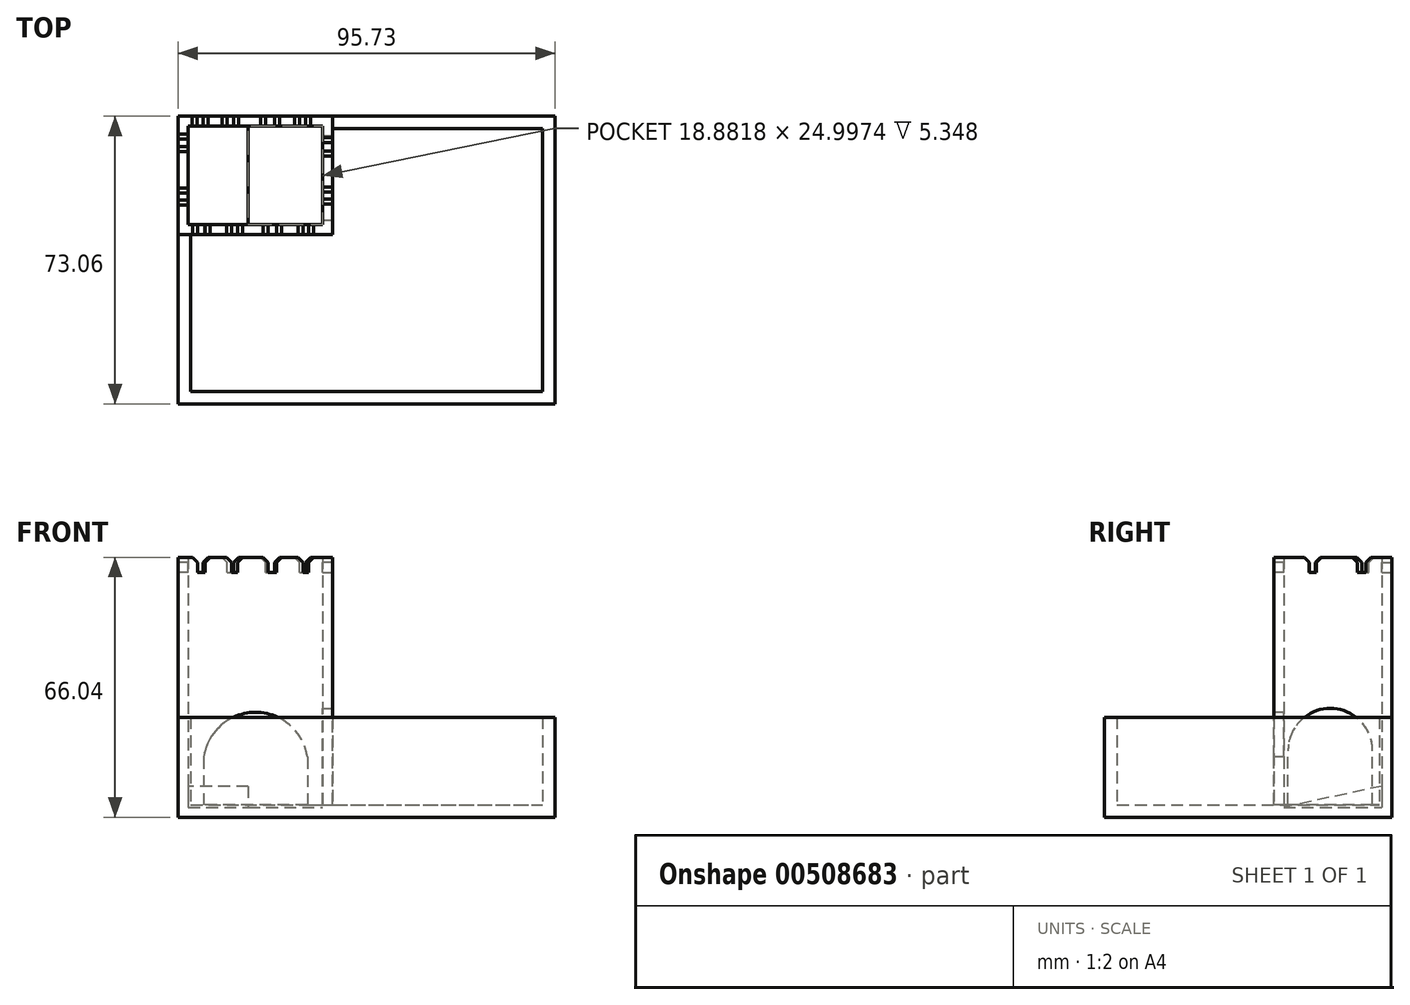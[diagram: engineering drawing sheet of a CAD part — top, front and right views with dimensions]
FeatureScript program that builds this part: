
annotation { "Feature Type Name" : "Feature", "Feature Type Description" : "" }
export const myFeature = defineFeature(function(context is Context, id is Id, definition is map)
    precondition{}
    {
        {
            var Q0;
            Q0=qCreatedBy(makeId("Top.planeOp"),FACE);
            var sketch = newSketch(context, id + "F0", { "sketchPlane" : qUnion([Q0])});
            skLineSegment(sketch, "E0.bottom", {"start": v(-43.95, -29.63) * mm, "end": v(51.78, -29.63) * mm});
            skLineSegment(sketch, "E0.top", {"start": v(-43.95, 43.43) * mm, "end": v(51.78, 43.43) * mm});
            skLineSegment(sketch, "E0.left", {"start": v(-43.95, -29.63) * mm, "end": v(-43.95, 43.43) * mm});
            skLineSegment(sketch, "E0.right", {"start": v(51.78, -29.63) * mm, "end": v(51.78, 43.43) * mm});
            skSolve(sketch);
        }
        {
            var Q0;
            Q0=makeQuery(id+"F0.imprint","IMPRINT",FACE,{"disambiguationData":[TD([[makeQuery(id+"F0.imprint","IMPRINT",EDGE,{"derivedFrom":sQuery(id+"F0.wireOp",EDGE,"E0.bottom")}),1.0]])]});
            extrude(context, id + "F1", {"entities" : qUnion([Q0]), "depth" : 25.4 * mm});
        }
        {
            var Q0;
            Q0=makeQuery(id+"F1.opExtrude","CAP_FACE",FACE,{"disambiguationData":[OSD([sQuery(id+"F0.wireOp",EDGE,"E0.bottom"),sQuery(id+"F0.wireOp",EDGE,"E0.top"),sQuery(id+"F0.wireOp",EDGE,"E0.left"),sQuery(id+"F0.wireOp",EDGE,"E0.right")])],"isStart":false});
            shell(context, id + "F2", {"entities" : qUnion([Q0]), "thickness" : 3.17 * mm});
        }
        {
            var Q0;
            Q0=makeQuery(id+"F2.opShell","OFFSET_FACE",FACE,{"disambiguationData":[OSD([sQuery(id+"F0.wireOp",EDGE,"E0.bottom"),sQuery(id+"F0.wireOp",EDGE,"E0.top"),sQuery(id+"F0.wireOp",EDGE,"E0.left"),sQuery(id+"F0.wireOp",EDGE,"E0.right")])]});
            var sketch = newSketch(context, id + "F3", { "sketchPlane" : qUnion([Q0])});
            skLineSegment(sketch, "E1.bottom", {"start": v(-40.77, 40.26) * mm, "end": v(-4.75, 40.26) * mm});
            skLineSegment(sketch, "E1.top", {"start": v(-40.77, 13.35) * mm, "end": v(-4.75, 13.35) * mm});
            skLineSegment(sketch, "E1.left", {"start": v(-40.77, 40.26) * mm, "end": v(-40.77, 13.35) * mm});
            skLineSegment(sketch, "E1.right", {"start": v(-4.75, 40.26) * mm, "end": v(-4.75, 13.35) * mm});
            skSolve(sketch);
        }
        {
            var Q0;
            Q0 = qSketchRegion(id + "F3", true);
            var Q1;
            Q1=makeQuery(id+"F3.imprint","IMPRINT",FACE,{"disambiguationData":[TD([[makeQuery(id+"F3.imprint","IMPRINT",EDGE,{"derivedFrom":sQuery(id+"F3.wireOp",EDGE,"E1.bottom")}),-1.0]])]});
            extrude(context, id + "F4", {"entities" : qUnion([Q0, Q1]), "operationType" : NewBodyOperationType.ADD, "depth" : 22.22 * mm});
        }
        {
            var Q0;
            Q0=makeQuery(id+"F4.boolean.opBoolean","MERGE",FACE,{"derivedFrom":[makeQuery(id+"F1.opExtrude","CAP_FACE",FACE,{"disambiguationData":[OSD([sQuery(id+"F0.wireOp",EDGE,"E0.bottom"),sQuery(id+"F0.wireOp",EDGE,"E0.top"),sQuery(id+"F0.wireOp",EDGE,"E0.left"),sQuery(id+"F0.wireOp",EDGE,"E0.right")])],"isStart":false}),makeQuery(id+"F4.opExtrude","CAP_FACE",FACE,{"disambiguationData":[OSD([sQuery(id+"F3.wireOp",EDGE,"E1.bottom"),sQuery(id+"F3.wireOp",EDGE,"E1.top"),sQuery(id+"F3.wireOp",EDGE,"E1.left"),sQuery(id+"F3.wireOp",EDGE,"E1.right")])],"isStart":false})]});
            var sketch = newSketch(context, id + "F5", { "sketchPlane" : qUnion([Q0])});
            skLineSegment(sketch, "E2", {"start": v(-40.77, 13.35) * mm, "end": v(-43.95, 13.35) * mm});
            skLineSegment(sketch, "E3", {"start": v(-4.75, 40.26) * mm, "end": v(-4.75, 43.43) * mm});
            skSolve(sketch);
        }
        {
            var Q0;
            Q0 = qSketchRegion(id + "F5", true);
            var Q1;
            {var subQ1=sQuery(id+"F5.wireOp",EDGE,"E2");Q1=makeQuery(id+"F5.imprint","IMPRINT",FACE,{"disambiguationData":[TD([[makeQuery(id+"F5.imprint","IMPRINT",EDGE,{"derivedFrom":subQ1}),-1.0]])]});}
            extrude(context, id + "F6", {"entities" : qUnion([Q0, Q1]), "operationType" : NewBodyOperationType.ADD, "depth" : 38.1 * mm});
        }
        {
            var Q0;
            Q0=makeQuery(id+"F6.opExtrude","CAP_FACE",FACE,{"disambiguationData":[OSD([sQuery(id+"F0.wireOp",EDGE,"E0.top"),sQuery(id+"F0.wireOp",EDGE,"E0.left"),sQuery(id+"F3.wireOp",EDGE,"E1.top"),sQuery(id+"F3.wireOp",EDGE,"E1.right"),sQuery(id+"F5.wireOp",EDGE,"E2"),sQuery(id+"F5.wireOp",EDGE,"E3")])],"isStart":false});
            shell(context, id + "F7", {"entities" : qUnion([Q0]), "thickness" : 2.54 * mm});
        }
        {
            var Q0;
            {var subQ0=sQuery(id+"F3.wireOp",EDGE,"E1.top");Q0=makeQuery(id+"F6.boolean.opBoolean","MERGE",FACE,{"derivedFrom":[makeQuery(id+"F4.opExtrude","SWEPT_FACE",FACE,{"disambiguationData":[OSD([subQ0])]}),makeQuery(id+"F6.opExtrude","SWEPT_FACE",FACE,{"disambiguationData":[OSD([subQ0,sQuery(id+"F5.wireOp",EDGE,"E2")])]})]});}
            var sketch = newSketch(context, id + "F8", { "sketchPlane" : qUnion([Q0])});
            skLineSegment(sketch, "E4.bottom", {"start": v(-37.47, 3.18) * mm, "end": v(-11.12, 3.18) * mm});
            skLineSegment(sketch, "E4.top", {"start": v(-37.47, 15.27) * mm, "end": v(-11.12, 15.27) * mm});
            skLineSegment(sketch, "E4.left", {"start": v(-37.47, 3.18) * mm, "end": v(-37.47, 15.27) * mm});
            skLineSegment(sketch, "E4.right", {"start": v(-11.12, 3.18) * mm, "end": v(-11.12, 15.27) * mm});
            skArc(sketch, "E5", {"start": v(-11.12, 15.27) * mm, "mid": v(-24.3, 26.67) * mm, "end": v(-37.47, 15.27) * mm});
            skSolve(sketch);
        }
        {
            var Q0;
            Q0=makeQuery(id+"F8.imprint","IMPRINT",FACE,{"disambiguationData":[TD([[makeQuery(id+"F8.imprint","IMPRINT",EDGE,{"derivedFrom":sQuery(id+"F8.wireOp",EDGE,"E4.top")}),1.0]])]});
            var Q1;
            Q1=makeQuery(id+"F8.imprint","IMPRINT",FACE,{"disambiguationData":[TD([[makeQuery(id+"F8.imprint","IMPRINT",EDGE,{"derivedFrom":sQuery(id+"F8.wireOp",EDGE,"E4.bottom")}),1.0]])]});
            extrude(context, id + "F9", {"entities" : qUnion([Q0, Q1]), "operationType" : NewBodyOperationType.REMOVE, "oppositeDirection" : true, "depth" : 3.17 * mm});
        }
        {
            var Q0;
            {var subQ0=sQuery(id+"F3.wireOp",EDGE,"E1.right");Q0=makeQuery(id+"F6.boolean.opBoolean","MERGE",FACE,{"derivedFrom":[makeQuery(id+"F4.opExtrude","SWEPT_FACE",FACE,{"disambiguationData":[OSD([subQ0])]}),makeQuery(id+"F6.opExtrude","SWEPT_FACE",FACE,{"disambiguationData":[OSD([subQ0,sQuery(id+"F5.wireOp",EDGE,"E3")])]})]});}
            var sketch = newSketch(context, id + "F10", { "sketchPlane" : qUnion([Q0])});
            skLineSegment(sketch, "E6.bottom", {"start": v(38.49, 3.18) * mm, "end": v(17, 3.18) * mm});
            skLineSegment(sketch, "E6.top", {"start": v(38.49, 16.91) * mm, "end": v(17, 16.91) * mm});
            skLineSegment(sketch, "E6.left", {"start": v(38.49, 3.18) * mm, "end": v(38.49, 16.91) * mm});
            skLineSegment(sketch, "E6.right", {"start": v(17, 3.18) * mm, "end": v(17, 16.91) * mm});
            skArc(sketch, "E7", {"start": v(38.49, 16.91) * mm, "mid": v(27.75, 27.66) * mm, "end": v(17, 16.91) * mm});
            skSolve(sketch);
        }
        {
            var Q0;
            Q0=makeQuery(id+"F10.imprint","IMPRINT",FACE,{"disambiguationData":[TD([[makeQuery(id+"F10.imprint","IMPRINT",EDGE,{"derivedFrom":sQuery(id+"F10.wireOp",EDGE,"E6.top")}),-1.0]])]});
            var Q1;
            Q1=makeQuery(id+"F10.imprint","IMPRINT",FACE,{"disambiguationData":[TD([[makeQuery(id+"F10.imprint","IMPRINT",EDGE,{"derivedFrom":sQuery(id+"F10.wireOp",EDGE,"E6.bottom")}),-1.0]])]});
            extrude(context, id + "F11", {"entities" : qUnion([Q0, Q1]), "operationType" : NewBodyOperationType.REMOVE, "oppositeDirection" : true, "depth" : 3.17 * mm});
        }
        {
            var Q0;
            Q0=makeQuery(id+"F7.opShell","OFFSET_FACE",FACE,{"disambiguationData":[OSD([sQuery(id+"F0.wireOp",EDGE,"E0.left")])]});
            var sketch = newSketch(context, id + "F12", { "sketchPlane" : qUnion([Q0])});
            skLineSegment(sketch, "E8", {"start": v(40.9, 7.89) * mm, "end": v(15.9, 2.54) * mm});
            skSolve(sketch);
        }
        {
            var Q0;
            Q0=makeQuery(id+"F6.opExtrude","CAP_FACE",FACE,{"disambiguationData":[OSD([sQuery(id+"F0.wireOp",EDGE,"E0.top"),sQuery(id+"F0.wireOp",EDGE,"E0.left"),sQuery(id+"F3.wireOp",EDGE,"E1.top"),sQuery(id+"F3.wireOp",EDGE,"E1.right"),sQuery(id+"F5.wireOp",EDGE,"E2"),sQuery(id+"F5.wireOp",EDGE,"E3")])],"isStart":false});
            var sketch = newSketch(context, id + "F13", { "sketchPlane" : qUnion([Q0])});
            skLineSegment(sketch, "E9.bottom", {"start": v(-39, 15.9) * mm, "end": v(-37.16, 15.9) * mm});
            skLineSegment(sketch, "E9.top", {"start": v(-39, 13.35) * mm, "end": v(-37.16, 13.35) * mm});
            skLineSegment(sketch, "E9.left", {"start": v(-39, 15.9) * mm, "end": v(-39, 13.35) * mm});
            skLineSegment(sketch, "E9.right", {"start": v(-37.16, 15.9) * mm, "end": v(-37.16, 13.35) * mm});
            skLineSegment(sketch, "E10.bottom", {"start": v(-30.36, 15.9) * mm, "end": v(-28.91, 15.9) * mm});
            skLineSegment(sketch, "E10.top", {"start": v(-30.36, 13.35) * mm, "end": v(-28.91, 13.35) * mm});
            skLineSegment(sketch, "E10.left", {"start": v(-30.36, 15.9) * mm, "end": v(-30.36, 13.35) * mm});
            skLineSegment(sketch, "E10.right", {"start": v(-28.91, 15.9) * mm, "end": v(-28.91, 13.35) * mm});
            skLineSegment(sketch, "E11.bottom", {"start": v(-10.8, 15.9) * mm, "end": v(-12.26, 15.9) * mm});
            skLineSegment(sketch, "E11.top", {"start": v(-10.8, 13.35) * mm, "end": v(-12.26, 13.35) * mm});
            skLineSegment(sketch, "E11.left", {"start": v(-10.8, 15.9) * mm, "end": v(-10.8, 13.35) * mm});
            skLineSegment(sketch, "E11.right", {"start": v(-12.26, 15.9) * mm, "end": v(-12.26, 13.35) * mm});
            skLineSegment(sketch, "E12.bottom", {"start": v(-19, 15.9) * mm, "end": v(-21.1, 15.9) * mm});
            skLineSegment(sketch, "E12.top", {"start": v(-19, 13.35) * mm, "end": v(-21.1, 13.35) * mm});
            skLineSegment(sketch, "E12.left", {"start": v(-19, 15.9) * mm, "end": v(-19, 13.35) * mm});
            skLineSegment(sketch, "E12.right", {"start": v(-21.1, 15.9) * mm, "end": v(-21.1, 13.35) * mm});
            skLineSegment(sketch, "E13.bottom", {"start": v(-41.4, 22.12) * mm, "end": v(-43.95, 22.12) * mm});
            skLineSegment(sketch, "E13.top", {"start": v(-41.4, 23.95) * mm, "end": v(-43.95, 23.95) * mm});
            skLineSegment(sketch, "E13.left", {"start": v(-41.4, 22.12) * mm, "end": v(-41.4, 23.95) * mm});
            skLineSegment(sketch, "E13.right", {"start": v(-43.95, 22.12) * mm, "end": v(-43.95, 23.95) * mm});
            skLineSegment(sketch, "E14.bottom", {"start": v(-41.4, 37.58) * mm, "end": v(-43.95, 37.58) * mm});
            skLineSegment(sketch, "E14.top", {"start": v(-41.4, 35.75) * mm, "end": v(-43.95, 35.75) * mm});
            skLineSegment(sketch, "E14.left", {"start": v(-41.4, 37.58) * mm, "end": v(-41.4, 35.75) * mm});
            skLineSegment(sketch, "E14.right", {"start": v(-43.95, 37.58) * mm, "end": v(-43.95, 35.75) * mm});
            skLineSegment(sketch, "E15.bottom", {"start": v(-39.09, 40.9) * mm, "end": v(-37.68, 40.9) * mm});
            skLineSegment(sketch, "E15.top", {"start": v(-39.09, 43.43) * mm, "end": v(-37.68, 43.43) * mm});
            skLineSegment(sketch, "E15.left", {"start": v(-39.09, 40.9) * mm, "end": v(-39.09, 43.43) * mm});
            skLineSegment(sketch, "E15.right", {"start": v(-37.68, 40.9) * mm, "end": v(-37.68, 43.43) * mm});
            skLineSegment(sketch, "E16.bottom", {"start": v(-31.53, 40.9) * mm, "end": v(-29.85, 40.9) * mm});
            skLineSegment(sketch, "E16.top", {"start": v(-31.53, 43.43) * mm, "end": v(-29.85, 43.43) * mm});
            skLineSegment(sketch, "E16.left", {"start": v(-31.53, 40.9) * mm, "end": v(-31.53, 43.43) * mm});
            skLineSegment(sketch, "E16.right", {"start": v(-29.85, 40.9) * mm, "end": v(-29.85, 43.43) * mm});
            skLineSegment(sketch, "E17.bottom", {"start": v(-21.73, 40.9) * mm, "end": v(-19.47, 40.9) * mm});
            skLineSegment(sketch, "E17.top", {"start": v(-21.73, 43.43) * mm, "end": v(-19.47, 43.43) * mm});
            skLineSegment(sketch, "E17.left", {"start": v(-21.73, 40.9) * mm, "end": v(-21.73, 43.43) * mm});
            skLineSegment(sketch, "E17.right", {"start": v(-19.47, 40.9) * mm, "end": v(-19.47, 43.43) * mm});
            skLineSegment(sketch, "E18.bottom", {"start": v(-11.54, 40.9) * mm, "end": v(-13.05, 40.9) * mm});
            skLineSegment(sketch, "E18.top", {"start": v(-11.54, 43.43) * mm, "end": v(-13.05, 43.43) * mm});
            skLineSegment(sketch, "E18.left", {"start": v(-11.54, 40.9) * mm, "end": v(-11.54, 43.43) * mm});
            skLineSegment(sketch, "E18.right", {"start": v(-13.05, 40.9) * mm, "end": v(-13.05, 43.43) * mm});
            skLineSegment(sketch, "E19.bottom", {"start": v(-7.29, 36.74) * mm, "end": v(-4.75, 36.74) * mm});
            skLineSegment(sketch, "E19.top", {"start": v(-7.29, 34.57) * mm, "end": v(-4.75, 34.57) * mm});
            skLineSegment(sketch, "E19.left", {"start": v(-7.29, 36.74) * mm, "end": v(-7.29, 34.57) * mm});
            skLineSegment(sketch, "E19.right", {"start": v(-4.75, 36.74) * mm, "end": v(-4.75, 34.57) * mm});
            skLineSegment(sketch, "E20.bottom", {"start": v(-7.29, 24.22) * mm, "end": v(-4.75, 24.22) * mm});
            skLineSegment(sketch, "E20.top", {"start": v(-7.29, 22.38) * mm, "end": v(-4.75, 22.38) * mm});
            skLineSegment(sketch, "E20.left", {"start": v(-7.29, 24.22) * mm, "end": v(-7.29, 22.38) * mm});
            skLineSegment(sketch, "E20.right", {"start": v(-4.75, 24.22) * mm, "end": v(-4.75, 22.38) * mm});
            skSolve(sketch);
        }
        {
            var Q0;
            Q0 = qSketchRegion(id + "F13", true);
            var Q1;
            Q1=makeQuery(id+"F13.imprint","IMPRINT",FACE,{"disambiguationData":[TD([[makeQuery(id+"F13.imprint","IMPRINT",EDGE,{"derivedFrom":sQuery(id+"F13.wireOp",EDGE,"E13.bottom")}),-1.0]])]});
            extrude(context, id + "F14", {"entities" : qUnion([Q0, Q1]), "operationType" : NewBodyOperationType.REMOVE, "oppositeDirection" : true, "depth" : 1.27 * mm});
        }
        {
            var Q0;
            {var subQ0=sQuery(id+"F5.wireOp",EDGE,"E3");var subQ1=sQuery(id+"F3.wireOp",EDGE,"E1.right");var subQ2=sQuery(id+"F5.wireOp",EDGE,"E2");var subQ3=sQuery(id+"F3.wireOp",EDGE,"E1.top");Q0=makeQuery(id+"F14.boolean.opBoolean","SPLIT",FACE,{"disambiguationData":[TD([makeQuery(id+"F14.opExtrude","SWEPT_FACE",FACE,{"disambiguationData":[OSD([sQuery(id+"F13.wireOp",EDGE,"E11.left")])]})])],"derivedFrom":makeQuery(id+"F6.opExtrude","CAP_FACE",FACE,{"disambiguationData":[OSD([sQuery(id+"F0.wireOp",EDGE,"E0.top"),sQuery(id+"F0.wireOp",EDGE,"E0.left"),subQ3,subQ1,subQ2,subQ0])],"isStart":false})});}
            var Q1;
            {var subQ0=sQuery(id+"F5.wireOp",EDGE,"E3");var subQ1=sQuery(id+"F3.wireOp",EDGE,"E1.right");Q1=makeQuery(id+"F14.boolean.opBoolean","SPLIT",FACE,{"disambiguationData":[TD([makeQuery(id+"F14.opExtrude","SWEPT_FACE",FACE,{"disambiguationData":[OSD([sQuery(id+"F13.wireOp",EDGE,"E19.top")])]})])],"derivedFrom":makeQuery(id+"F6.opExtrude","CAP_FACE",FACE,{"disambiguationData":[OSD([sQuery(id+"F0.wireOp",EDGE,"E0.top"),sQuery(id+"F0.wireOp",EDGE,"E0.left"),sQuery(id+"F3.wireOp",EDGE,"E1.top"),subQ1,sQuery(id+"F5.wireOp",EDGE,"E2"),subQ0])],"isStart":false})});}
            var Q2;
            {var subQ0=sQuery(id+"F0.wireOp",EDGE,"E0.top");var subQ1=sQuery(id+"F5.wireOp",EDGE,"E3");var subQ2=sQuery(id+"F3.wireOp",EDGE,"E1.right");Q2=makeQuery(id+"F14.boolean.opBoolean","SPLIT",FACE,{"disambiguationData":[TD([makeQuery(id+"F14.opExtrude","SWEPT_FACE",FACE,{"disambiguationData":[OSD([sQuery(id+"F13.wireOp",EDGE,"E18.left")])]})])],"derivedFrom":makeQuery(id+"F6.opExtrude","CAP_FACE",FACE,{"disambiguationData":[OSD([subQ0,sQuery(id+"F0.wireOp",EDGE,"E0.left"),sQuery(id+"F3.wireOp",EDGE,"E1.top"),subQ2,sQuery(id+"F5.wireOp",EDGE,"E2"),subQ1])],"isStart":false})});}
            var Q3;
            {var subQ0=sQuery(id+"F0.wireOp",EDGE,"E0.top");Q3=makeQuery(id+"F14.boolean.opBoolean","SPLIT",FACE,{"disambiguationData":[TD([makeQuery(id+"F14.opExtrude","SWEPT_FACE",FACE,{"disambiguationData":[OSD([sQuery(id+"F13.wireOp",EDGE,"E17.right")])]})])],"derivedFrom":makeQuery(id+"F6.opExtrude","CAP_FACE",FACE,{"disambiguationData":[OSD([subQ0,sQuery(id+"F0.wireOp",EDGE,"E0.left"),sQuery(id+"F3.wireOp",EDGE,"E1.top"),sQuery(id+"F3.wireOp",EDGE,"E1.right"),sQuery(id+"F5.wireOp",EDGE,"E2"),sQuery(id+"F5.wireOp",EDGE,"E3")])],"isStart":false})});}
            var Q4;
            {var subQ0=sQuery(id+"F0.wireOp",EDGE,"E0.top");Q4=makeQuery(id+"F14.boolean.opBoolean","SPLIT",FACE,{"disambiguationData":[TD([makeQuery(id+"F14.opExtrude","SWEPT_FACE",FACE,{"disambiguationData":[OSD([sQuery(id+"F13.wireOp",EDGE,"E16.right")])]})])],"derivedFrom":makeQuery(id+"F6.opExtrude","CAP_FACE",FACE,{"disambiguationData":[OSD([subQ0,sQuery(id+"F0.wireOp",EDGE,"E0.left"),sQuery(id+"F3.wireOp",EDGE,"E1.top"),sQuery(id+"F3.wireOp",EDGE,"E1.right"),sQuery(id+"F5.wireOp",EDGE,"E2"),sQuery(id+"F5.wireOp",EDGE,"E3")])],"isStart":false})});}
            var Q5;
            {var subQ0=sQuery(id+"F0.wireOp",EDGE,"E0.top");Q5=makeQuery(id+"F14.boolean.opBoolean","SPLIT",FACE,{"disambiguationData":[TD([makeQuery(id+"F14.opExtrude","SWEPT_FACE",FACE,{"disambiguationData":[OSD([sQuery(id+"F13.wireOp",EDGE,"E15.right")])]})])],"derivedFrom":makeQuery(id+"F6.opExtrude","CAP_FACE",FACE,{"disambiguationData":[OSD([subQ0,sQuery(id+"F0.wireOp",EDGE,"E0.left"),sQuery(id+"F3.wireOp",EDGE,"E1.top"),sQuery(id+"F3.wireOp",EDGE,"E1.right"),sQuery(id+"F5.wireOp",EDGE,"E2"),sQuery(id+"F5.wireOp",EDGE,"E3")])],"isStart":false})});}
            var Q6;
            {var subQ0=sQuery(id+"F0.wireOp",EDGE,"E0.top");var subQ1=sQuery(id+"F0.wireOp",EDGE,"E0.left");Q6=makeQuery(id+"F14.boolean.opBoolean","SPLIT",FACE,{"disambiguationData":[TD([makeQuery(id+"F14.opExtrude","SWEPT_FACE",FACE,{"disambiguationData":[OSD([sQuery(id+"F13.wireOp",EDGE,"E14.bottom")])]})])],"derivedFrom":makeQuery(id+"F6.opExtrude","CAP_FACE",FACE,{"disambiguationData":[OSD([subQ0,subQ1,sQuery(id+"F3.wireOp",EDGE,"E1.top"),sQuery(id+"F3.wireOp",EDGE,"E1.right"),sQuery(id+"F5.wireOp",EDGE,"E2"),sQuery(id+"F5.wireOp",EDGE,"E3")])],"isStart":false})});}
            var Q7;
            {var subQ0=sQuery(id+"F0.wireOp",EDGE,"E0.left");Q7=makeQuery(id+"F14.boolean.opBoolean","SPLIT",FACE,{"disambiguationData":[TD([makeQuery(id+"F14.opExtrude","SWEPT_FACE",FACE,{"disambiguationData":[OSD([sQuery(id+"F13.wireOp",EDGE,"E13.top")])]})])],"derivedFrom":makeQuery(id+"F6.opExtrude","CAP_FACE",FACE,{"disambiguationData":[OSD([sQuery(id+"F0.wireOp",EDGE,"E0.top"),subQ0,sQuery(id+"F3.wireOp",EDGE,"E1.top"),sQuery(id+"F3.wireOp",EDGE,"E1.right"),sQuery(id+"F5.wireOp",EDGE,"E2"),sQuery(id+"F5.wireOp",EDGE,"E3")])],"isStart":false})});}
            var Q8;
            {var subQ0=sQuery(id+"F0.wireOp",EDGE,"E0.left");var subQ1=sQuery(id+"F5.wireOp",EDGE,"E2");var subQ2=sQuery(id+"F3.wireOp",EDGE,"E1.top");Q8=makeQuery(id+"F14.boolean.opBoolean","SPLIT",FACE,{"disambiguationData":[TD([makeQuery(id+"F14.opExtrude","SWEPT_FACE",FACE,{"disambiguationData":[OSD([sQuery(id+"F13.wireOp",EDGE,"E9.left")])]})])],"derivedFrom":makeQuery(id+"F6.opExtrude","CAP_FACE",FACE,{"disambiguationData":[OSD([sQuery(id+"F0.wireOp",EDGE,"E0.top"),subQ0,subQ2,sQuery(id+"F3.wireOp",EDGE,"E1.right"),subQ1,sQuery(id+"F5.wireOp",EDGE,"E3")])],"isStart":false})});}
            var Q9;
            {var subQ0=sQuery(id+"F5.wireOp",EDGE,"E2");var subQ1=sQuery(id+"F3.wireOp",EDGE,"E1.top");Q9=makeQuery(id+"F14.boolean.opBoolean","SPLIT",FACE,{"disambiguationData":[TD([makeQuery(id+"F14.opExtrude","SWEPT_FACE",FACE,{"disambiguationData":[OSD([sQuery(id+"F13.wireOp",EDGE,"E9.right")])]})])],"derivedFrom":makeQuery(id+"F6.opExtrude","CAP_FACE",FACE,{"disambiguationData":[OSD([sQuery(id+"F0.wireOp",EDGE,"E0.top"),sQuery(id+"F0.wireOp",EDGE,"E0.left"),subQ1,sQuery(id+"F3.wireOp",EDGE,"E1.right"),subQ0,sQuery(id+"F5.wireOp",EDGE,"E3")])],"isStart":false})});}
            var Q10;
            {var subQ0=sQuery(id+"F5.wireOp",EDGE,"E2");var subQ1=sQuery(id+"F3.wireOp",EDGE,"E1.top");Q10=makeQuery(id+"F14.boolean.opBoolean","SPLIT",FACE,{"disambiguationData":[TD([makeQuery(id+"F14.opExtrude","SWEPT_FACE",FACE,{"disambiguationData":[OSD([sQuery(id+"F13.wireOp",EDGE,"E10.right")])]})])],"derivedFrom":makeQuery(id+"F6.opExtrude","CAP_FACE",FACE,{"disambiguationData":[OSD([sQuery(id+"F0.wireOp",EDGE,"E0.top"),sQuery(id+"F0.wireOp",EDGE,"E0.left"),subQ1,sQuery(id+"F3.wireOp",EDGE,"E1.right"),subQ0,sQuery(id+"F5.wireOp",EDGE,"E3")])],"isStart":false})});}
            var Q11;
            {var subQ0=sQuery(id+"F5.wireOp",EDGE,"E2");var subQ1=sQuery(id+"F3.wireOp",EDGE,"E1.top");Q11=makeQuery(id+"F14.boolean.opBoolean","SPLIT",FACE,{"disambiguationData":[TD([makeQuery(id+"F14.opExtrude","SWEPT_FACE",FACE,{"disambiguationData":[OSD([sQuery(id+"F13.wireOp",EDGE,"E11.right")])]})])],"derivedFrom":makeQuery(id+"F6.opExtrude","CAP_FACE",FACE,{"disambiguationData":[OSD([sQuery(id+"F0.wireOp",EDGE,"E0.top"),sQuery(id+"F0.wireOp",EDGE,"E0.left"),subQ1,sQuery(id+"F3.wireOp",EDGE,"E1.right"),subQ0,sQuery(id+"F5.wireOp",EDGE,"E3")])],"isStart":false})});}
            extrude(context, id + "F15", {"entities" : qUnion([Q0, Q1, Q2, Q3, Q4, Q5, Q6, Q7, Q8, Q9, Q10, Q11]), "operationType" : NewBodyOperationType.ADD, "depth" : 2.54 * mm});
        }
        {
            var Q0;
            Q0=makeQuery(id+"F15.opExtrude","CAP_EDGE",EDGE,{"disambiguationData":[OSD([sQuery(id+"F13.wireOp",EDGE,"E11.left")])],"isStart":false});
            var Q1;
            Q1=makeQuery(id+"F15.opExtrude","CAP_EDGE",EDGE,{"disambiguationData":[OSD([sQuery(id+"F13.wireOp",EDGE,"E11.right")])],"isStart":false});
            chamfer(context, id + "F16", {"entities" : qUnion([Q0, Q1]), "width" : 1.27 * mm, "tangentPropagation" : true});
        }
        {
            var Q0;
            Q0=makeQuery(id+"F15.opExtrude","CAP_EDGE",EDGE,{"disambiguationData":[OSD([sQuery(id+"F13.wireOp",EDGE,"E20.top")])],"isStart":false});
            var Q1;
            Q1=makeQuery(id+"F15.opExtrude","CAP_EDGE",EDGE,{"disambiguationData":[OSD([sQuery(id+"F13.wireOp",EDGE,"E20.bottom")])],"isStart":false});
            var Q2;
            Q2=makeQuery(id+"F15.opExtrude","CAP_EDGE",EDGE,{"disambiguationData":[OSD([sQuery(id+"F13.wireOp",EDGE,"E19.top")])],"isStart":false});
            var Q3;
            Q3=makeQuery(id+"F15.opExtrude","CAP_EDGE",EDGE,{"disambiguationData":[OSD([sQuery(id+"F13.wireOp",EDGE,"E19.bottom")])],"isStart":false});
            chamfer(context, id + "F17", {"entities" : qUnion([Q0, Q1, Q2, Q3]), "width" : 1.27 * mm, "tangentPropagation" : true});
        }
        {
            var Q0;
            Q0=makeQuery(id+"F15.opExtrude","CAP_EDGE",EDGE,{"disambiguationData":[OSD([sQuery(id+"F13.wireOp",EDGE,"E18.left")])],"isStart":false});
            var Q1;
            Q1=makeQuery(id+"F15.opExtrude","CAP_EDGE",EDGE,{"disambiguationData":[OSD([sQuery(id+"F13.wireOp",EDGE,"E18.right")])],"isStart":false});
            var Q2;
            Q2=makeQuery(id+"F15.opExtrude","CAP_EDGE",EDGE,{"disambiguationData":[OSD([sQuery(id+"F13.wireOp",EDGE,"E17.right")])],"isStart":false});
            var Q3;
            Q3=makeQuery(id+"F15.opExtrude","CAP_EDGE",EDGE,{"disambiguationData":[OSD([sQuery(id+"F13.wireOp",EDGE,"E17.left")])],"isStart":false});
            var Q4;
            Q4=makeQuery(id+"F15.opExtrude","CAP_EDGE",EDGE,{"disambiguationData":[OSD([sQuery(id+"F13.wireOp",EDGE,"E15.left")])],"isStart":false});
            var Q5;
            Q5=makeQuery(id+"F15.opExtrude","CAP_EDGE",EDGE,{"disambiguationData":[OSD([sQuery(id+"F13.wireOp",EDGE,"E15.right")])],"isStart":false});
            var Q6;
            Q6=makeQuery(id+"F15.opExtrude","CAP_EDGE",EDGE,{"disambiguationData":[OSD([sQuery(id+"F13.wireOp",EDGE,"E16.left")])],"isStart":false});
            var Q7;
            Q7=makeQuery(id+"F15.opExtrude","CAP_EDGE",EDGE,{"disambiguationData":[OSD([sQuery(id+"F13.wireOp",EDGE,"E16.right")])],"isStart":false});
            chamfer(context, id + "F18", {"entities" : qUnion([Q0, Q1, Q2, Q3, Q4, Q5, Q6, Q7]), "width" : 1.27 * mm, "tangentPropagation" : true});
        }
        {
            var Q0;
            Q0=makeQuery(id+"F15.opExtrude","CAP_EDGE",EDGE,{"disambiguationData":[OSD([sQuery(id+"F13.wireOp",EDGE,"E14.bottom")])],"isStart":false});
            var Q1;
            Q1=makeQuery(id+"F15.opExtrude","CAP_EDGE",EDGE,{"disambiguationData":[OSD([sQuery(id+"F13.wireOp",EDGE,"E14.top")])],"isStart":false});
            var Q2;
            Q2=makeQuery(id+"F15.opExtrude","CAP_EDGE",EDGE,{"disambiguationData":[OSD([sQuery(id+"F13.wireOp",EDGE,"E13.top")])],"isStart":false});
            var Q3;
            Q3=makeQuery(id+"F15.opExtrude","CAP_EDGE",EDGE,{"disambiguationData":[OSD([sQuery(id+"F13.wireOp",EDGE,"E13.bottom")])],"isStart":false});
            var Q4;
            Q4=makeQuery(id+"F15.opExtrude","CAP_EDGE",EDGE,{"disambiguationData":[OSD([sQuery(id+"F13.wireOp",EDGE,"E9.left")])],"isStart":false});
            var Q5;
            Q5=makeQuery(id+"F15.opExtrude","CAP_EDGE",EDGE,{"disambiguationData":[OSD([sQuery(id+"F13.wireOp",EDGE,"E9.right")])],"isStart":false});
            var Q6;
            Q6=makeQuery(id+"F15.opExtrude","CAP_EDGE",EDGE,{"disambiguationData":[OSD([sQuery(id+"F13.wireOp",EDGE,"E10.left")])],"isStart":false});
            var Q7;
            Q7=makeQuery(id+"F15.opExtrude","CAP_EDGE",EDGE,{"disambiguationData":[OSD([sQuery(id+"F13.wireOp",EDGE,"E10.right")])],"isStart":false});
            var Q8;
            Q8=makeQuery(id+"F15.opExtrude","CAP_EDGE",EDGE,{"disambiguationData":[OSD([sQuery(id+"F13.wireOp",EDGE,"E12.right")])],"isStart":false});
            var Q9;
            Q9=makeQuery(id+"F15.opExtrude","CAP_EDGE",EDGE,{"disambiguationData":[OSD([sQuery(id+"F13.wireOp",EDGE,"E12.left")])],"isStart":false});
            chamfer(context, id + "F19", {"entities" : qUnion([Q0, Q1, Q2, Q3, Q4, Q5, Q6, Q7, Q8, Q9]), "width" : 1.27 * mm, "tangentPropagation" : true});
        }
        {
            var Q0;
            {var subQ0=sQuery(id+"F12.wireOp",EDGE,"E8");Q0=makeQuery(id+"F12.imprint","IMPRINT",FACE,{"disambiguationData":[TD([[makeQuery(id+"F12.imprint","IMPRINT",EDGE,{"derivedFrom":subQ0}),1.0]])]});}
            extrude(context, id + "F20", {"entities" : qUnion([Q0]), "operationType" : NewBodyOperationType.ADD, "depth" : 15.24 * mm});
        }
    });
